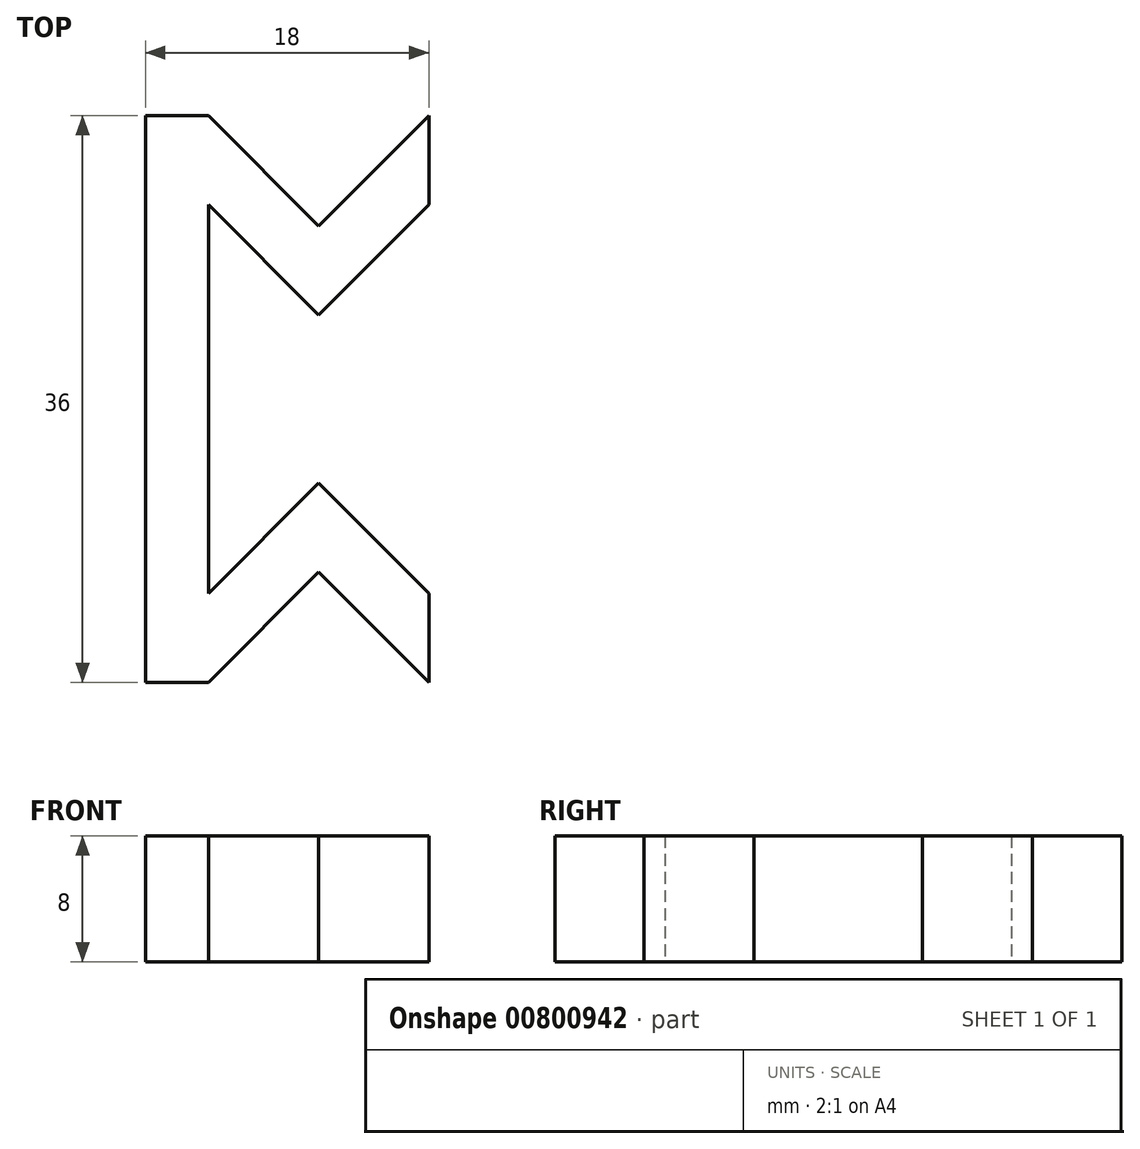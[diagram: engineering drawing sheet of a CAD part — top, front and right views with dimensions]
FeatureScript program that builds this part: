
annotation { "Feature Type Name" : "Feature", "Feature Type Description" : "" }
export const myFeature = defineFeature(function(context is Context, id is Id, definition is map)
    precondition{}
    {
        {
            var Q0;
            Q0=qCreatedBy(makeId("Top.planeOp"),FACE);
            var sketch = newSketch(context, id + "F0", { "sketchPlane" : qUnion([Q0])});
            skLineSegment(sketch, "E0", {"start": v(0, 0) * mm, "end": v(0, -36) * mm});
            skLineSegment(sketch, "E1", {"start": v(0, -36) * mm, "end": v(4, -36) * mm});
            skLineSegment(sketch, "E2", {"start": v(4, -36) * mm, "end": v(11, -29) * mm});
            skLineSegment(sketch, "E3", {"start": v(11, -29) * mm, "end": v(18, -36) * mm});
            skLineSegment(sketch, "E4", {"start": v(18, -36) * mm, "end": v(18, -30.34) * mm});
            skLineSegment(sketch, "E5", {"start": v(18, -30.34) * mm, "end": v(11, -23.34) * mm});
            skLineSegment(sketch, "E6", {"start": v(11, -23.34) * mm, "end": v(4, -30.34) * mm});
            skLineSegment(sketch, "E7", {"start": v(4, -5.66) * mm, "end": v(11, -12.66) * mm});
            skLineSegment(sketch, "E8", {"start": v(11, -12.66) * mm, "end": v(18, -5.66) * mm});
            skLineSegment(sketch, "E9", {"start": v(18, -5.66) * mm, "end": v(18, 0) * mm});
            skLineSegment(sketch, "E10", {"start": v(18, 0) * mm, "end": v(11, -7) * mm});
            skLineSegment(sketch, "E11", {"start": v(11, -7) * mm, "end": v(4, 0) * mm});
            skLineSegment(sketch, "E12", {"start": v(4, 0) * mm, "end": v(0, 0) * mm});
            skLineSegment(sketch, "E13", {"start": v(4, -5.66) * mm, "end": v(4, -30.34) * mm});
            skLineSegment(sketch, "E14", {"start": v(18, -30.34) * mm, "end": v(18, -5.66) * mm, "construction": true});
            skSolve(sketch);
        }
        {
            var Q0;
            Q0 = qSketchRegion(id + "F0", true);
            extrude(context, id + "F1", {"entities" : qUnion([Q0]), "depth" : 8 * mm, "offsetDistance" : 25 * mm});
        }
    });
